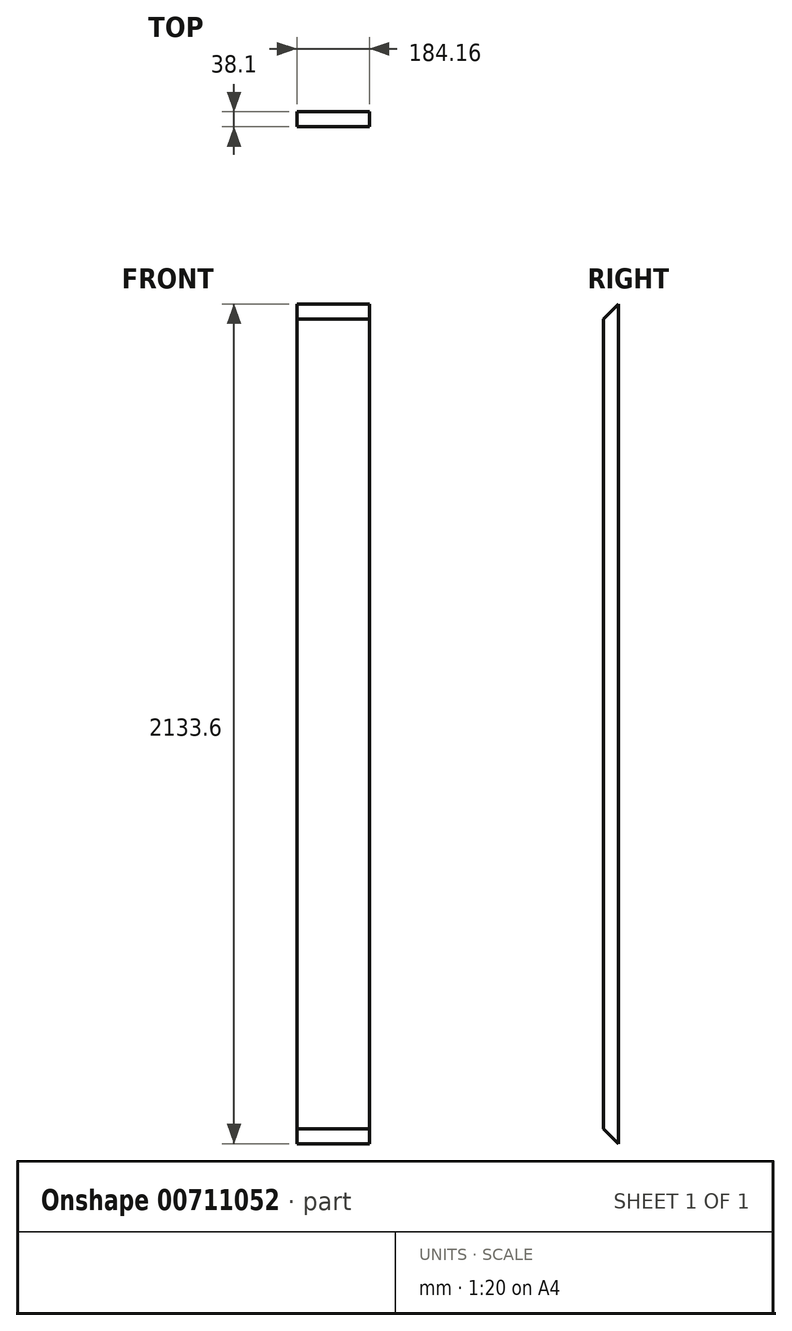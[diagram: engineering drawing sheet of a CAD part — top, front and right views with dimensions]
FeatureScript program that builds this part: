
annotation { "Feature Type Name" : "Feature", "Feature Type Description" : "" }
export const myFeature = defineFeature(function(context is Context, id is Id, definition is map)
    precondition{}
    {
        {
            var Q0;
            Q0=qCreatedBy(makeId("Top.planeOp"),FACE);
            var sketch = newSketch(context, id + "F0", { "sketchPlane" : qUnion([Q0])});
            skLineSegment(sketch, "E0.bottom", {"start": v(92.08, 19.05) * mm, "end": v(-92.08, 19.05) * mm});
            skLineSegment(sketch, "E0.top", {"start": v(92.08, -19.05) * mm, "end": v(-92.07, -19.05) * mm});
            skLineSegment(sketch, "E0.left", {"start": v(92.08, 19.05) * mm, "end": v(92.08, -19.05) * mm});
            skLineSegment(sketch, "E0.right", {"start": v(-92.08, 19.05) * mm, "end": v(-92.08, -19.05) * mm});
            skPoint(sketch, "E0.middle", {"position": v(0, 0) * mm});
            skSolve(sketch);
        }
        {
            var Q0;
            Q0=makeQuery(id+"F0.imprint","IMPRINT",FACE,{"disambiguationData":[TD([[makeQuery(id+"F0.imprint","IMPRINT",EDGE,{"derivedFrom":sQuery(id+"F0.wireOp",EDGE,"E0.bottom")}),1.0]])]});
            extrude(context, id + "F1", {"entities" : qUnion([Q0]), "depth" : 2133.6 * mm, "offsetDistance" : 25.4 * mm});
        }
        {
            var Q0;
            Q0=makeQuery(id+"F1.opExtrude","SWEPT_FACE",FACE,{"disambiguationData":[OSD([sQuery(id+"F0.wireOp",EDGE,"E0.right")])]});
            var sketch = newSketch(context, id + "F2", { "sketchPlane" : qUnion([Q0])});
            skLineSegment(sketch, "E1", {"start": v(-19.05, 2133.6) * mm, "end": v(19.05, 2095.5) * mm});
            skLineSegment(sketch, "E2", {"start": v(-19.05, 2133.6) * mm, "end": v(19.05, 2133.6) * mm});
            skLineSegment(sketch, "E3", {"start": v(19.05, 2133.6) * mm, "end": v(19.05, 2095.5) * mm});
            skLineSegment(sketch, "E4", {"start": v(-19.05, 0) * mm, "end": v(19.05, 38.1) * mm});
            skLineSegment(sketch, "E5", {"start": v(-19.05, 0) * mm, "end": v(19.05, 0) * mm});
            skLineSegment(sketch, "E6", {"start": v(19.05, 0) * mm, "end": v(19.05, 38.1) * mm});
            skSolve(sketch);
        }
        {
            var Q0;
            Q0 = qSketchRegion(id + "F2", true);
            extrude(context, id + "F3", {"entities" : qUnion([Q0]), "operationType" : NewBodyOperationType.REMOVE, "oppositeDirection" : true, "depth" : 190.5 * mm, "offsetDistance" : 25.4 * mm});
        }
    });
